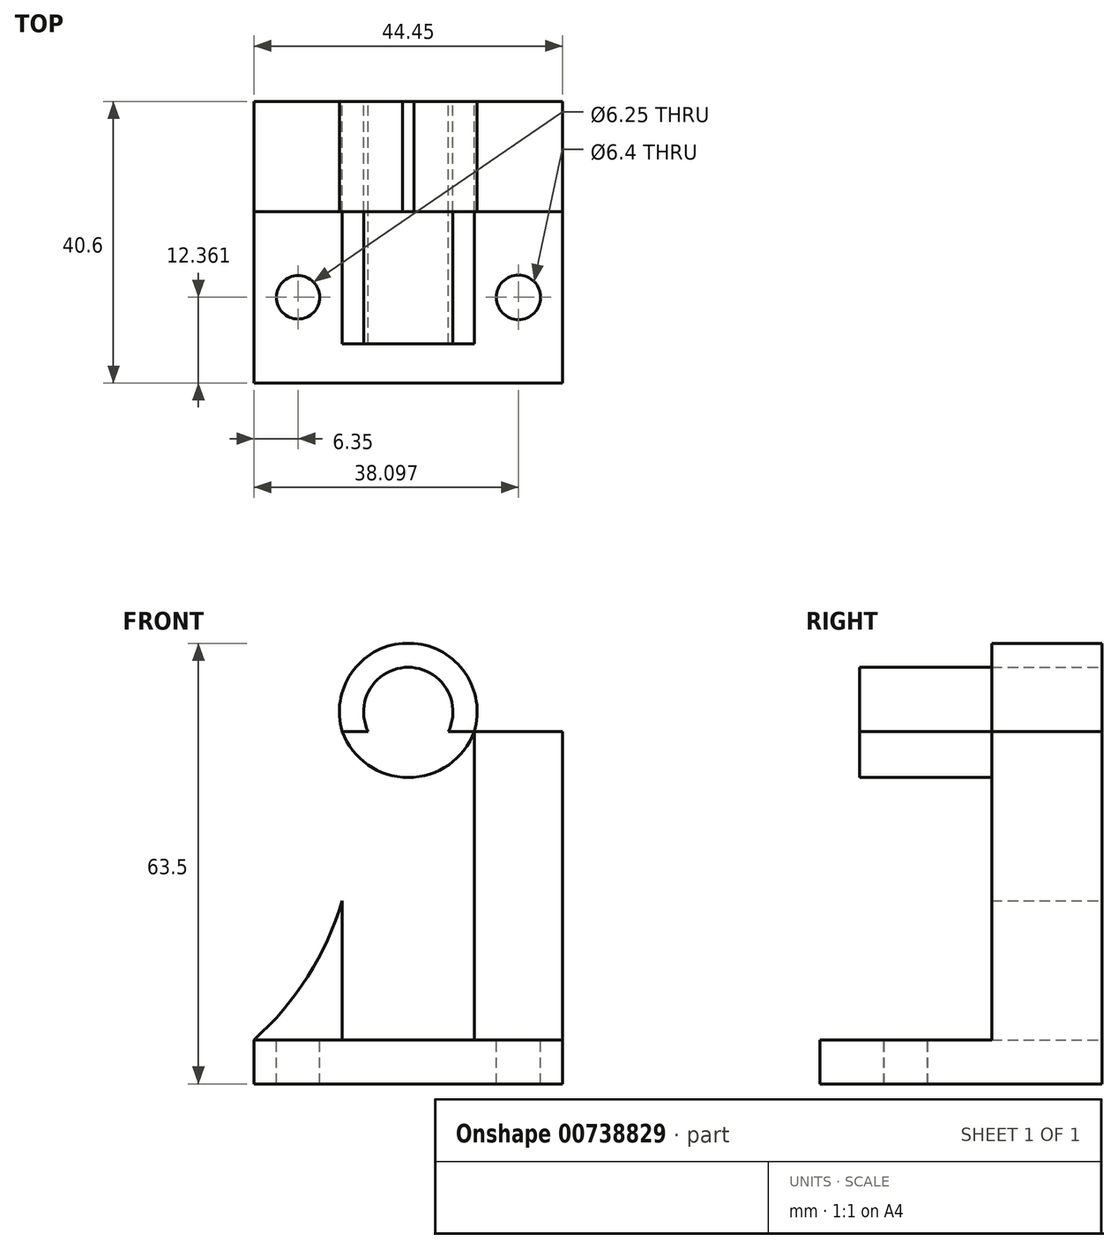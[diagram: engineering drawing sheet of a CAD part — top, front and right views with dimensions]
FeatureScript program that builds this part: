
annotation { "Feature Type Name" : "Feature", "Feature Type Description" : "" }
export const myFeature = defineFeature(function(context is Context, id is Id, definition is map)
    precondition{}
    {
        {
            var Q0;
            Q0=qCreatedBy(makeId("Front.planeOp"),FACE);
            var sketch = newSketch(context, id + "F0", { "sketchPlane" : qUnion([Q0])});
            skLineSegment(sketch, "E0", {"start": v(0, 0) * mm, "end": v(0, 63.5) * mm});
            skLineSegment(sketch, "E1", {"start": v(0, 63.5) * mm, "end": v(44.45, 63.5) * mm});
            skLineSegment(sketch, "E2", {"start": v(44.45, 63.5) * mm, "end": v(44.45, 0) * mm});
            skLineSegment(sketch, "E3", {"start": v(44.45, 0) * mm, "end": v(0, 0) * mm});
            skSolve(sketch);
        }
        {
            var Q0;
            Q0 = qSketchRegion(id + "F0", true);
            extrude(context, id + "F1", {"entities" : qUnion([Q0]), "depth" : 31.75 * mm, "offsetDistance" : 25.4 * mm});
        }
        {
            var Q0;
            Q0=makeQuery(id+"F1.opExtrude","CAP_FACE",FACE,{"disambiguationData":[OSD([sQuery(id+"F0.wireOp",EDGE,"E0"),sQuery(id+"F0.wireOp",EDGE,"E1"),sQuery(id+"F0.wireOp",EDGE,"E2"),sQuery(id+"F0.wireOp",EDGE,"E3")])],"isStart":true});
            var sketch = newSketch(context, id + "F2", { "sketchPlane" : qUnion([Q0])});
            skLineSegment(sketch, "E4", {"start": v(-44.45, 6.35) * mm, "end": v(0, 6.35) * mm});
            skLineSegment(sketch, "E5", {"start": v(-44.45, 50.8) * mm, "end": v(0, 50.8) * mm});
            skLineSegment(sketch, "E6", {"start": v(-31.75, 63.5) * mm, "end": v(-31.75, 0) * mm});
            skLineSegment(sketch, "E7", {"start": v(-12.7, 63.5) * mm, "end": v(-12.7, 0) * mm});
            skArc(sketch, "E8", {"start": v(-12.7, 50.8) * mm, "mid": v(-22.23, 63.53) * mm, "end": v(-31.75, 50.8) * mm});
            skArc(sketch, "E9", {"start": v(-31.75, 50.8) * mm, "mid": v(-31.65, 26.73) * mm, "end": v(-44.45, 6.35) * mm});
            skArc(sketch, "E10", {"start": v(-12.7, 50.8) * mm, "mid": v(-12.8, 26.73) * mm, "end": v(0, 6.35) * mm});
            skCircle(sketch, "E11", {"center": v(-22.23, 53.6) * mm, "radius": 6.43 * mm});
            skSolve(sketch);
        }
        {
            var Q0;
            {var subQ1=sQuery(id+"F2.wireOp",EDGE,"E6");var subQ6=makeQuery(id+"F1.opExtrude","CAP_EDGE",EDGE,{"disambiguationData":[OSD([sQuery(id+"F0.wireOp",EDGE,"E1")])],"isStart":true});var subQ8=makeQuery(id+"F2.imprint","INTERSECT",VERTEX,{"derivedFrom":[subQ6,subQ1]});Q0=makeQuery(id+"F2.imprint","IMPRINT",FACE,{"disambiguationData":[TD([[makeQuery(id+"F2.imprint","IMPRINT",EDGE,{"disambiguationData":[TD([[subQ8,-1.0]])],"derivedFrom":subQ1}),-1.0]])]});}
            var Q1;
            {var subQ0=sQuery(id+"F2.wireOp",EDGE,"E6");var subQ1=makeQuery(id+"F1.opExtrude","CAP_EDGE",EDGE,{"disambiguationData":[OSD([sQuery(id+"F0.wireOp",EDGE,"E1")])],"isStart":true});var subQ2=makeQuery(id+"F2.imprint","INTERSECT",VERTEX,{"derivedFrom":[subQ1,subQ0]});Q1=makeQuery(id+"F2.imprint","IMPRINT",FACE,{"disambiguationData":[TD([[makeQuery(id+"F2.imprint","IMPRINT",EDGE,{"disambiguationData":[TD([[subQ2,-1.0]])],"derivedFrom":subQ0}),1.0]])]});}
            var Q2;
            {var subQ0=sQuery(id+"F2.wireOp",EDGE,"E7");var subQ1=makeQuery(id+"F1.opExtrude","CAP_EDGE",EDGE,{"disambiguationData":[OSD([sQuery(id+"F0.wireOp",EDGE,"E1")])],"isStart":true});var subQ2=makeQuery(id+"F2.imprint","INTERSECT",VERTEX,{"derivedFrom":[subQ1,subQ0]});Q2=makeQuery(id+"F2.imprint","IMPRINT",FACE,{"disambiguationData":[TD([[makeQuery(id+"F2.imprint","IMPRINT",EDGE,{"disambiguationData":[TD([[subQ2,-1.0]])],"derivedFrom":subQ0}),-1.0]])]});}
            var Q3;
            {var subQ0=sQuery(id+"F2.wireOp",EDGE,"E11");var subQ1=sQuery(id+"F2.wireOp",EDGE,"E5");var subQ2=makeQuery(id+"F2.imprint","INTERSECT",VERTEX,{"disambiguationData":[OD(0.0)],"derivedFrom":[subQ1,subQ0]});Q3=makeQuery(id+"F2.imprint","IMPRINT",FACE,{"disambiguationData":[TD([[makeQuery(id+"F2.imprint","IMPRINT",EDGE,{"disambiguationData":[TD([[subQ2,-1.0]])],"derivedFrom":subQ1}),1.0]])]});}
            var Q4;
            {var subQ0=sQuery(id+"F2.wireOp",EDGE,"E11");var subQ1=sQuery(id+"F2.wireOp",EDGE,"E5");var subQ2=makeQuery(id+"F2.imprint","INTERSECT",VERTEX,{"disambiguationData":[OD(0.0)],"derivedFrom":[subQ1,subQ0]});Q4=makeQuery(id+"F2.imprint","IMPRINT",FACE,{"disambiguationData":[TD([[makeQuery(id+"F2.imprint","IMPRINT",EDGE,{"disambiguationData":[TD([[subQ2,-1.0]])],"derivedFrom":subQ1}),-1.0]])]});}
            var Q5;
            {var subQ0=makeQuery(id+"F1.opExtrude","CAP_EDGE",EDGE,{"disambiguationData":[OSD([sQuery(id+"F0.wireOp",EDGE,"E1")])],"isStart":true});var subQ6=sQuery(id+"F2.wireOp",EDGE,"E7");var subQ9=makeQuery(id+"F2.imprint","INTERSECT",VERTEX,{"derivedFrom":[subQ0,subQ6]});Q5=makeQuery(id+"F2.imprint","IMPRINT",FACE,{"disambiguationData":[TD([[makeQuery(id+"F2.imprint","IMPRINT",EDGE,{"disambiguationData":[TD([[subQ9,-1.0]])],"derivedFrom":subQ6}),1.0]])]});}
            var Q6;
            {var subQ3=sQuery(id+"F2.wireOp",EDGE,"E10");var subQ4=sQuery(id+"F2.wireOp",EDGE,"E7");var subQ6=makeQuery(id+"F2.imprint","INTERSECT",VERTEX,{"derivedFrom":[subQ4,subQ3]});Q6=makeQuery(id+"F2.imprint","IMPRINT",FACE,{"disambiguationData":[TD([[makeQuery(id+"F2.imprint","IMPRINT",EDGE,{"disambiguationData":[TD([[subQ6,-1.0]])],"derivedFrom":subQ3}),1.0]])]});}
            var Q7;
            {var subQ0=sQuery(id+"F2.wireOp",EDGE,"E10");var subQ1=sQuery(id+"F2.wireOp",EDGE,"E7");var subQ3=makeQuery(id+"F2.imprint","INTERSECT",VERTEX,{"derivedFrom":[subQ1,subQ0]});Q7=makeQuery(id+"F2.imprint","IMPRINT",FACE,{"disambiguationData":[TD([[makeQuery(id+"F2.imprint","IMPRINT",EDGE,{"disambiguationData":[TD([[subQ3,1.0]])],"derivedFrom":subQ1}),-1.0]])]});}
            var Q8;
            {var subQ0=sQuery(id+"F2.wireOp",EDGE,"E9");var subQ1=sQuery(id+"F2.wireOp",EDGE,"E6");var subQ3=makeQuery(id+"F2.imprint","INTERSECT",VERTEX,{"derivedFrom":[subQ1,subQ0]});Q8=makeQuery(id+"F2.imprint","IMPRINT",FACE,{"disambiguationData":[TD([[makeQuery(id+"F2.imprint","IMPRINT",EDGE,{"disambiguationData":[TD([[subQ3,1.0]])],"derivedFrom":subQ1}),1.0]])]});}
            var Q9;
            {var subQ3=sQuery(id+"F2.wireOp",EDGE,"E9");var subQ4=sQuery(id+"F2.wireOp",EDGE,"E6");var subQ6=makeQuery(id+"F2.imprint","INTERSECT",VERTEX,{"derivedFrom":[subQ4,subQ3]});Q9=makeQuery(id+"F2.imprint","IMPRINT",FACE,{"disambiguationData":[TD([[makeQuery(id+"F2.imprint","IMPRINT",EDGE,{"disambiguationData":[TD([[subQ6,-1.0]])],"derivedFrom":subQ3}),-1.0]])]});}
            extrude(context, id + "F3", {"entities" : qUnion([Q0, Q1, Q2, Q3, Q4, Q5, Q6, Q7, Q8, Q9]), "operationType" : NewBodyOperationType.REMOVE, "endBound" : BoundingType.THROUGH_ALL, "oppositeDirection" : true, "depth" : 25.4 * mm, "offsetDistance" : 25.4 * mm});
        }
        {
            var Q0;
            Q0=makeQuery(id+"F1.opExtrude","SWEPT_FACE",FACE,{"disambiguationData":[OSD([sQuery(id+"F0.wireOp",EDGE,"E3")])]});
            var sketch = newSketch(context, id + "F4", { "sketchPlane" : qUnion([Q0])});
            skLineSegment(sketch, "E12", {"start": v(0, 15.88) * mm, "end": v(44.45, 15.88) * mm});
            skSolve(sketch);
        }
        {
            var Q0;
            {var subQ0=sQuery(id+"F4.wireOp",EDGE,"E12");Q0=makeQuery(id+"F4.imprint","IMPRINT",FACE,{"disambiguationData":[TD([[makeQuery(id+"F4.imprint","IMPRINT",EDGE,{"derivedFrom":subQ0}),1.0]])]});}
            extrude(context, id + "F5", {"entities" : qUnion([Q0]), "operationType" : NewBodyOperationType.REMOVE, "endBound" : BoundingType.THROUGH_ALL, "oppositeDirection" : true, "depth" : 25.4 * mm, "offsetDistance" : 25.4 * mm});
        }
        {
            var Q0;
            Q0=qCreatedBy(makeId("Top.planeOp"),FACE);
            var sketch = newSketch(context, id + "F6", { "sketchPlane" : qUnion([Q0])});
            skLineSegment(sketch, "E13", {"start": v(0, -15.85) * mm, "end": v(0, -40.6) * mm});
            skLineSegment(sketch, "E14", {"start": v(44.45, -15.78) * mm, "end": v(44.45, -40.6) * mm});
            skLineSegment(sketch, "E15", {"start": v(0, -40.6) * mm, "end": v(44.45, -40.6) * mm});
            skLineSegment(sketch, "E16", {"start": v(0, -15.85) * mm, "end": v(44.45, -15.78) * mm});
            skSolve(sketch);
        }
        {
            var Q0;
            Q0 = qSketchRegion(id + "F6", true);
            extrude(context, id + "F7", {"entities" : qUnion([Q0]), "operationType" : NewBodyOperationType.ADD, "depth" : 6.35 * mm, "offsetDistance" : 25.4 * mm});
        }
        {
            var Q0;
            Q0=makeQuery(id+"F5.boolean.opBoolean","COPY",FACE,{"derivedFrom":makeQuery(id+"F5.opExtrude","SWEPT_FACE",FACE,{"disambiguationData":[OSD([sQuery(id+"F4.wireOp",EDGE,"E12")])]})});
            var sketch = newSketch(context, id + "F8", { "sketchPlane" : qUnion([Q0])});
            skArc(sketch, "E17", {"start": v(12.7, 50.8) * mm, "mid": v(22.23, 44.15) * mm, "end": v(31.75, 50.8) * mm});
            skSolve(sketch);
        }
        {
            var Q0;
            Q0=makeQuery(id+"F8.imprint","IMPRINT",FACE,{"disambiguationData":[TD([[makeQuery(id+"F8.imprint","IMPRINT",EDGE,{"derivedFrom":sQuery(id+"F8.wireOp",EDGE,"E17")}),1.0]])]});
            extrude(context, id + "F9", {"entities" : qUnion([Q0]), "operationType" : NewBodyOperationType.ADD, "depth" : 19.05 * mm, "offsetDistance" : 25.4 * mm});
        }
        {
            var Q0;
            Q0=makeQuery(id+"F7.opExtrude","CAP_FACE",FACE,{"disambiguationData":[OSD([sQuery(id+"F6.wireOp",EDGE,"E13"),sQuery(id+"F6.wireOp",EDGE,"E14"),sQuery(id+"F6.wireOp",EDGE,"E15"),sQuery(id+"F6.wireOp",EDGE,"E16")])],"isStart":false});
            var sketch = newSketch(context, id + "F10", { "sketchPlane" : qUnion([Q0])});
            skLineSegment(sketch, "E18", {"start": v(0, -28.24) * mm, "end": v(44.45, -28.24) * mm});
            skLineSegment(sketch, "E19", {"start": v(6.35, -15.88) * mm, "end": v(6.35, -40.6) * mm});
            skLineSegment(sketch, "E20", {"start": v(38.1, -15.88) * mm, "end": v(38.1, -40.6) * mm});
            skCircle(sketch, "E21", {"center": v(6.35, -28.24) * mm, "radius": 3.13 * mm});
            skCircle(sketch, "E22", {"center": v(38.1, -28.24) * mm, "radius": 3.2 * mm});
            skSolve(sketch);
        }
        {
            var Q0;
            Q0 = qSketchRegion(id + "F10", true);
            extrude(context, id + "F11", {"entities" : qUnion([Q0]), "operationType" : NewBodyOperationType.REMOVE, "endBound" : BoundingType.THROUGH_ALL, "oppositeDirection" : true, "depth" : 25.4 * mm, "offsetDistance" : 25.4 * mm});
        }
    });
